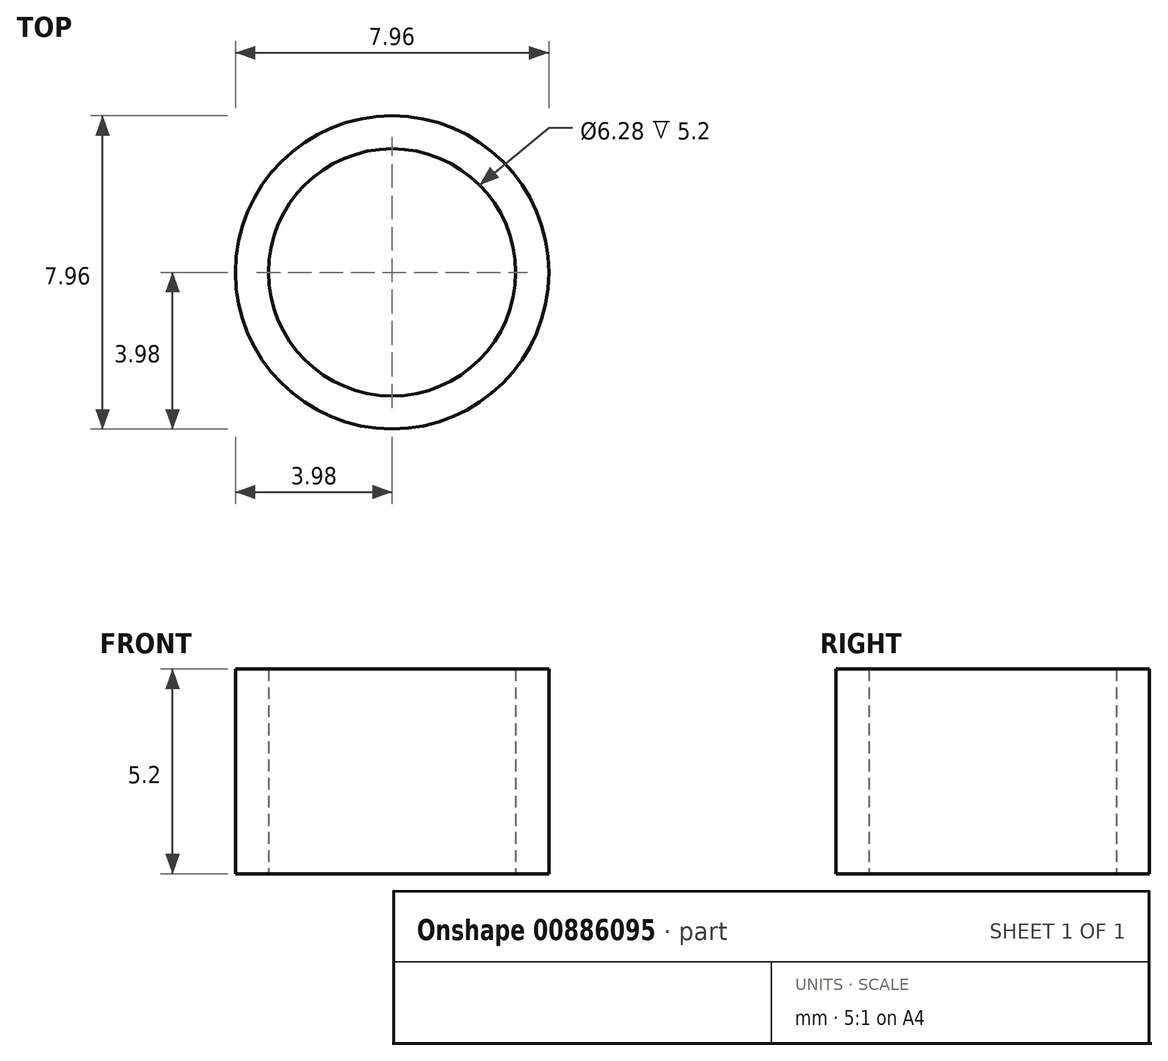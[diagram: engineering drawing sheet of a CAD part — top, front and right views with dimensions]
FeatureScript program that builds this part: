
annotation { "Feature Type Name" : "Feature", "Feature Type Description" : "" }
export const myFeature = defineFeature(function(context is Context, id is Id, definition is map)
    precondition{}
    {
        {
            var Q0;
            Q0=qCreatedBy(makeId("Top.planeOp"),FACE);
            var sketch = newSketch(context, id + "F0", { "sketchPlane" : qUnion([Q0])});
            skCircle(sketch, "E0", {"center": v(0, 0) * mm, "radius": 3.98 * mm});
            skCircle(sketch, "E1", {"center": v(0, 0) * mm, "radius": 3.14 * mm});
            skSolve(sketch);
        }
        {
            var Q0;
            Q0=makeQuery(id+"F0.imprint","IMPRINT",FACE,{"disambiguationData":[TD([[makeQuery(id+"F0.imprint","IMPRINT",EDGE,{"derivedFrom":sQuery(id+"F0.wireOp",EDGE,"E0")}),1.0]])]});
            extrude(context, id + "F1", {"entities" : qUnion([Q0]), "depth" : 5.2 * mm, "offsetDistance" : 25 * mm});
        }
    });
